# Revit family: 变频给水泵
name_source: partatom
category: 机械设备
units: mm (PartAtom-declared; Revit-internal decimal feet)

## family parameters
共享 = 否
加载时剪切的空心 = 否
圆形连接件大小 = 使用直径
基于工作平面 = 否
总是垂直 = 是
房间计算点 = 否
零件类型 = 标准

## types (2) — shared parameters
URL = www.goujianwu.com
净重 = 275.00 kg
出水口位置 = 84  [stored 0.275591 ft]
出水口法兰外半径 = 93
出水口长度 = 260  [stored 0.853018 ft]
出水口高度 = 270  [stored 0.885827 ft]
吸水口法兰外半径 = 100  [stored 0.328084 ft]
吸水口长度 = 260  [stored 0.853018 ft]
吸水口高度 = 140  [stored 0.459318 ft]
底座宽度 = 300
底座长度 = 300
底座高度 = 50  [stored 0.164042 ft]
极数 = 1
水泵材质 = M-金属漆-蓝色
电压 = 0 V
给排水工作压力 = 400000.0 Pa
螺栓位置 = 250  [stored 0.82021 ft]
螺栓间距 = 250  [stored 0.82021 ft]
说明 = 找构件就上构件坞
高度 = 1040  [stored 3.41207 ft]
zero-valued in all types: 默认高程

## per-type parameters (varying)
| type | 出水口公称半径 | 出水口公称直径 | 功率 | 吸水口公称半径 | 吸水口公称直径 | 流量 |
| 20m³/h-60m-7.5KW | 40  [stored 0.131234 ft] | 80  [stored 0.262467 ft] | 7500 W | 40  [stored 0.131234 ft] | 80  [stored 0.262467 ft] | 20.0 L/s |
| 55m³/h-60m-15KW | 75  [stored 0.246063 ft] | 150  [stored 0.492126 ft] | 15000 W | 75  [stored 0.246063 ft] | 150  [stored 0.492126 ft] | 55.0 L/s |

note: [stored X ft] marks values corroborated as IEEE doubles in the binary element streams (Revit-internal decimal feet)
